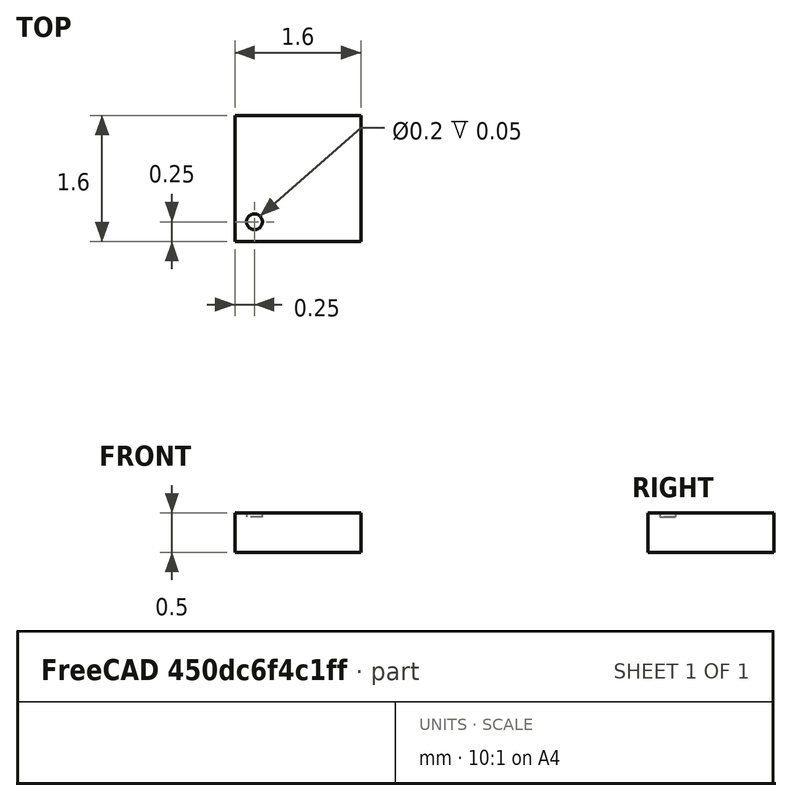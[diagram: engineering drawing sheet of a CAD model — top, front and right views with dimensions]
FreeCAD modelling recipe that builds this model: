
FCSTD DOCUMENT  (FreeCAD 1.0R39319 (Git))
Label: DFN3L_1.6x1.6
License: All rights reserved
LicenseURL: http://en.wikipedia.org/wiki/All_rights_reserved
objects: Part::Box×1, PartDesign::FeatureBase×1, PartDesign::Body×1, Part::Cylinder×1, Part::Cut×1, App::Part×1
note: 6 computed .brp shape members not serialized (recipe doc carries the construction recipe); baked Part::Feature solids carry a one-line shape summary decoded from their .brp

FEATURE [Part::Box] Box  label="Cube"
  AttacherType = Attacher::AttachEngine3D
  Height = 0.5
  Length = 1.6
  Width = 1.6
FEATURE [PartDesign::FeatureBase] BaseFeature
  BaseFeature = -> Box
  Suppressed = false
FEATURE [PartDesign::Body] Body
  AllowCompound = false
  BaseFeature = -> Box
  Group = -> [BaseFeature]
  Origin = -> Origin
  Tip = -> BaseFeature
FEATURE [Part::Cylinder] Cylinder
  Angle = 360
  AttacherType = Attacher::AttachEngine3D
  FirstAngle = 0
  Height = 0.5
  Placement = pos=(0.25,0.25,0.45) rot=(0,0,1;0rad)
  Radius = 0.1
  SecondAngle = 0
FEATURE [Part::Cut] Cut
  Base = -> Box
  Tool = -> Cylinder
FEATURE [App::Part] Part
  Group = -> [Box,Cylinder,Cut]
  Origin = -> Origin001
